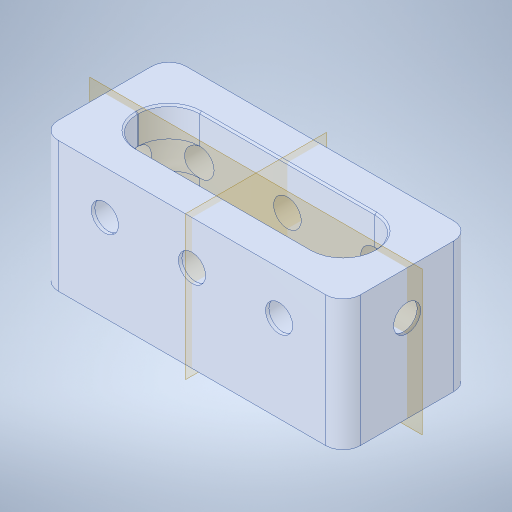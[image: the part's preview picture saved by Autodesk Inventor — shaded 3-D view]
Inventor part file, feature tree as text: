
AUTODESK INVENTOR PART (.ipt)
format: ipt  version: 2023.4 (Build 274418000, 418)  size: 473,600 bytes
history: native  units: in
note: dims shown in document units (in); Inventor stores cm internally (conversion verified against a paired STEP export)
features: sketch x5, hole x3, projected_geometry x3, extrude x2, chamfer x1
ambient origin geometry x8: Origin, YZ Plane, XZ Plane, XY Plane, X Axis, Y Axis, Z Axis, Center Point
bodies: Solid1 (feature_tree)
feature tree (14):
  extrude  "Extrusion1"  Depth=1.0in TaperAngle=0.0deg
  hole  "Hole1"  [1 undecoded]
  hole  "Hole2"  [1 undecoded]
  hole  "Hole3"  [1 undecoded]
  extrude  "Extrusion2"  [1 undecoded]
  sketch  "Sketch1"  dims[d0=0.0625in d1=1.0in d2=0.0in]
  projected_geometry  "Projected Loop1"
  sketch  "Sketch2"  dims[d3=0.156in d4=0.38in d5=0.385in d6=0.25in d7=0.563in d8=1.0in d9=0.8108in]
  projected_geometry  "Projected Loop2"
  sketch  "Sketch3"  dims[d10=0.196in d11=0.5in d12=0.375in d13=0.25in d14=0.5635in d15=1.0in d16=0.8108in]
  sketch  "Sketch4"  dims[d17=0.156in d18=0.38in d19=0.385in d20=0.25in d21=0.563in d22=1.0in d23=0.8108in d24=0.0625in]
  sketch  "Sketch5"  dims[d25=1.0in d26=0.0in d27=0.5in d28=1.9685in]
  projected_geometry  "Projected Loop3"
  chamfer  "Chamfer2"  [1 undecoded]
note: 5 required parameter values undecoded (feature->parameter linkage not recoverable at this tier; creation-order binding heuristic only, values carry confidence <= 0.55)
